# Revit family: BuzziMoon
name_source: partatom
category: Lighting Fixtures
revit_build: Autodesk Revit 2018 (Build: 20180329_1100(x64)
units: mm (PartAtom-declared; Revit-internal decimal feet)

## family parameters
Always vertical = Yes
Cut with Voids When Loaded = No
Host = Ceiling
Light Source = Yes
OmniClass Number = 23.80.70.11
OmniClass Title = Luminaries for Internal Lighting
Part Type = Normal
Room Calculation Point = No
Round Connector Dimension = Use Diameter
Shared = No

## types (18) — shared parameters
Cable Material = <By Category>
Color Filter = 16777215
Dimming Lamp Color Temperature Shift = <None>
Fixture Material = <By Category>
Lens = <By Category>
Light Source Symbol Size = 2' - 0"

## per-type parameters (varying)
| type | 3D Drop L | 3D Drop M | 3D Drop S | 3D Leaf L | 3D Leaf M | 3D Leaf S | 3D Rib L | 3D Rib M | 3D Rib S | Fixture Height AFF | Flat L | Flat M | Flat S | Oval |
| 3D Drop L | Yes | No | No | No | No | No | No | No | No | 3' - 0" | No | No | No | No |
| 3D Drop M | No | Yes | No | No | No | No | No | No | No | 3' - 0" | No | No | No | No |
| 3D Drop S | No | No | Yes | No | No | No | No | No | No | 3' - 0" | No | No | No | No |
| 3D Leaf L | No | No | No | Yes | No | No | No | No | No | 3' - 0" | No | No | No | No |
| 3D Leaf M | No | No | No | No | Yes | No | No | No | No | 3' - 0" | No | No | No | No |
| 3D Leaf S | No | No | No | No | No | Yes | No | No | No | 3' - 0" | No | No | No | No |
| 3D Rib L | No | No | No | No | No | No | Yes | No | No | 3' - 0" | No | No | No | No |
| 3D Rib M | No | No | No | No | No | No | No | Yes | No | 3' - 0" | No | No | No | No |
| 3D Rib S | No | No | No | No | No | No | No | No | Yes | 3' - 0" | No | No | No | No |
| Flat L | No | No | No | No | No | No | No | No | No | 3' - 0" | Yes | No | No | No |
| Flat M | No | No | No | No | No | No | No | No | No | 3' - 0" | No | Yes | No | No |
| Oval 3D Leaf M | No | No | No | No | No | No | No | No | No | 3' - 0" | No | No | No | Yes |
| Oval 3D Leaf S | No | No | No | No | No | No | No | No | No | 3' - 0" | No | No | No | Yes |
| Oval 3D Rib M | No | No | No | No | No | No | No | No | No | 3' - 0" | No | No | No | Yes |
| Oval 3D Rib S | No | No | No | No | No | No | No | No | No | 3' - 0" | No | No | No | Yes |
| Oval Flat M | No | No | No | No | No | No | No | No | No | 3' - 0" | No | No | No | Yes |
| Oval Flat S | No | No | No | No | No | No | No | No | No | 5' - 0" | No | No | No | Yes |
| Flat S | No | No | No | No | No | No | No | No | No | 5' - 0" | No | No | Yes | No |

type visibility flags (boolean, named after types; folded from table):
- 3D Drop L: Yes: (none)
- 3D Drop M: Yes: (none)
- 3D Drop S: Yes: (none)
- 3D Leaf L: Yes: (none)
- 3D Leaf M: Yes: (none)
- 3D Leaf S: Yes: (none)
- 3D Rib L: Yes: (none)
- 3D Rib M: Yes: (none)
- 3D Rib S: Yes: (none)
- Flat L: Yes: (none)
- Flat M: Yes: (none)
- Oval 3D Leaf M: Yes: Oval 3D Leaf M
- Oval 3D Leaf S: Yes: Oval 3D Leaf S
- Oval 3D Rib M: Yes: Oval 3D Rib M
- Oval 3D Rib S: Yes: Oval 3D Rib S
- Oval Flat M: Yes: Oval Flat M
- Oval Flat S: Yes: Oval Flat S
- Flat S: Yes: (none)

## geometry (parser evidence)
native form markers: Sweep x42
no freeform markers — native parametric forms only
